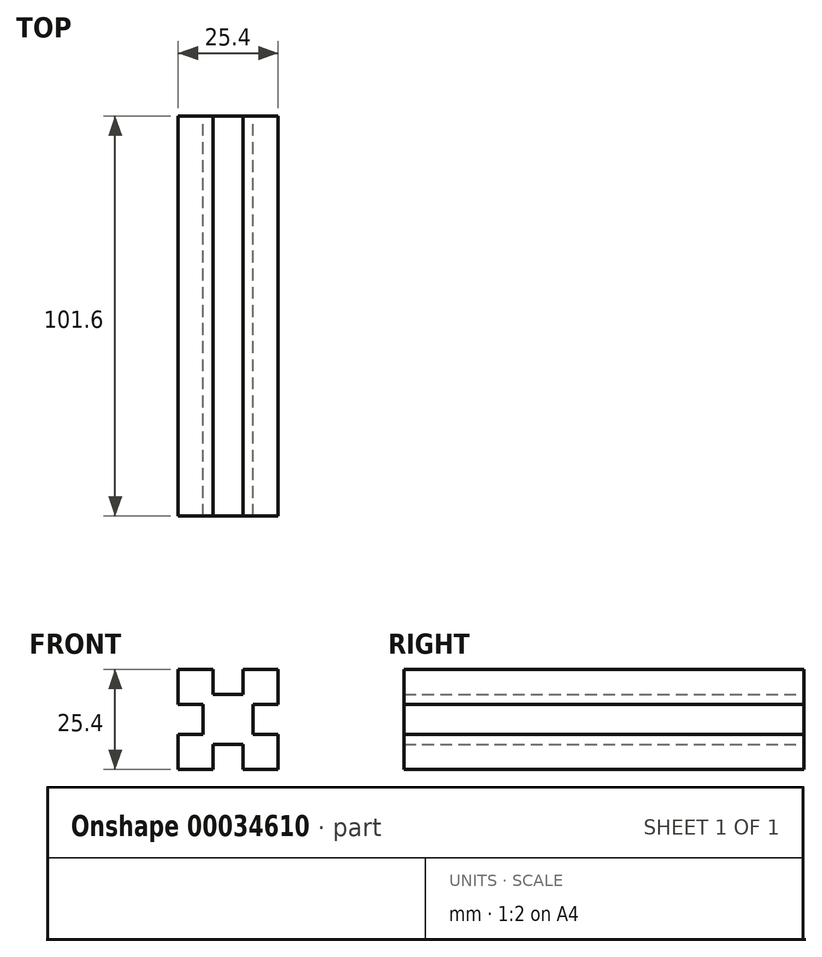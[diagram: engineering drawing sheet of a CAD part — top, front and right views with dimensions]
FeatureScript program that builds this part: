
annotation { "Feature Type Name" : "Feature", "Feature Type Description" : "" }
export const myFeature = defineFeature(function(context is Context, id is Id, definition is map)
    precondition{}
    {
        {
            var Q0;
            Q0=qCreatedBy(makeId("Front.planeOp"),FACE);
            var sketch = newSketch(context, id + "F0", { "sketchPlane" : qUnion([Q0])});
            skLineSegment(sketch, "E0.bottom", {"start": v(0, 0) * mm, "end": v(8.9, 0) * mm});
            skLineSegment(sketch, "E0.top", {"start": v(0, 25.4) * mm, "end": v(8.89, 25.4) * mm});
            skLineSegment(sketch, "E0.left", {"start": v(0, 0) * mm, "end": v(0, 8.9) * mm});
            skLineSegment(sketch, "E0.right", {"start": v(25.4, 0) * mm, "end": v(25.4, 8.89) * mm});
            skLineSegment(sketch, "E1.top", {"start": v(8.89, 19.05) * mm, "end": v(16.51, 19.05) * mm});
            skLineSegment(sketch, "E1.left", {"start": v(8.89, 25.4) * mm, "end": v(8.89, 19.05) * mm});
            skLineSegment(sketch, "E1.right", {"start": v(16.51, 25.4) * mm, "end": v(16.51, 19.05) * mm});
            skLineSegment(sketch, "E2.bottom", {"start": v(0, 16.5) * mm, "end": v(6.35, 16.5) * mm});
            skLineSegment(sketch, "E2.top", {"start": v(0, 8.9) * mm, "end": v(6.35, 8.9) * mm});
            skLineSegment(sketch, "E2.right", {"start": v(6.35, 16.5) * mm, "end": v(6.35, 8.9) * mm});
            skLineSegment(sketch, "E3.bottom", {"start": v(8.89, 6.35) * mm, "end": v(16.5, 6.35) * mm});
            skLineSegment(sketch, "E3.left", {"start": v(8.9, 6.35) * mm, "end": v(8.9, 0) * mm});
            skLineSegment(sketch, "E3.right", {"start": v(16.5, 6.35) * mm, "end": v(16.5, 0) * mm});
            skLineSegment(sketch, "E4.bottom", {"start": v(19.05, 16.5) * mm, "end": v(25.4, 16.5) * mm});
            skLineSegment(sketch, "E4.top", {"start": v(19.05, 8.89) * mm, "end": v(25.4, 8.89) * mm});
            skLineSegment(sketch, "E4.left", {"start": v(19.05, 16.5) * mm, "end": v(19.05, 8.89) * mm});
            skLineSegment(sketch, "E5.trimOffspring", {"start": v(0, 16.5) * mm, "end": v(0, 25.4) * mm});
            skLineSegment(sketch, "E6.trimOffspring", {"start": v(25.4, 16.5) * mm, "end": v(25.4, 25.4) * mm});
            skLineSegment(sketch, "E7.trimOffspring", {"start": v(16.5, 0) * mm, "end": v(25.4, 0) * mm});
            skLineSegment(sketch, "E8.trimOffspring", {"start": v(16.51, 25.4) * mm, "end": v(25.4, 25.4) * mm});
            skSolve(sketch);
        }
        {
            var Q0;
            Q0=qSketchRegion(id+"F0",true);
            extrude(context, id + "F1", {"entities" : qUnion([Q0]), "depth" : 101.6 * mm});
        }
    });
